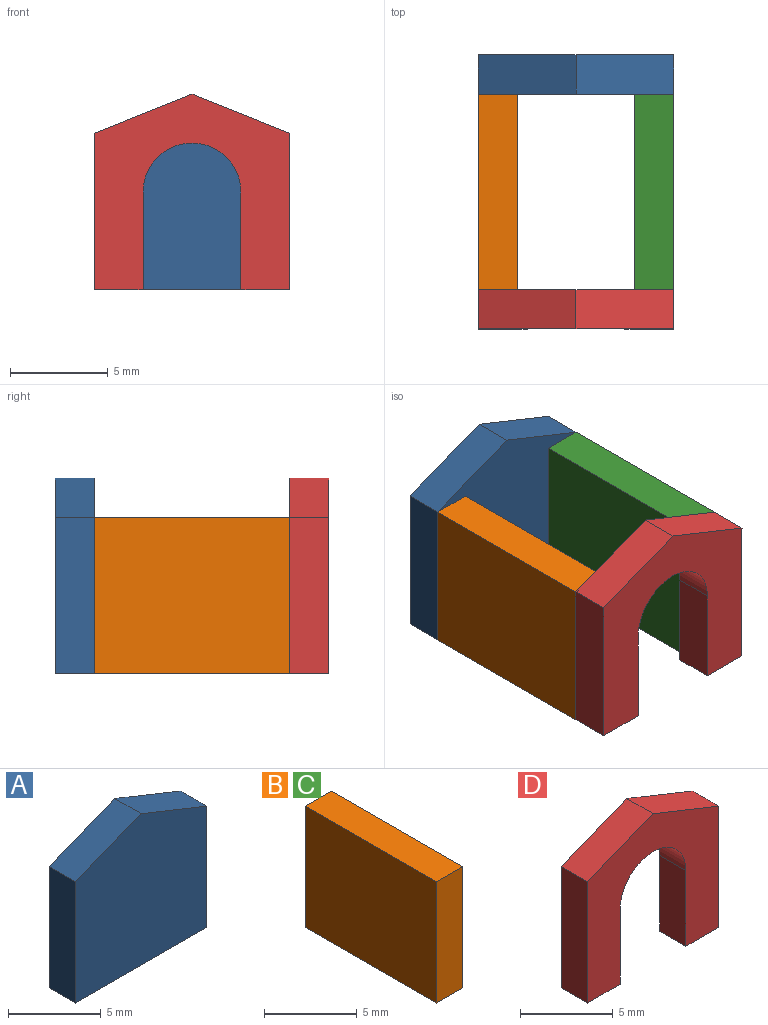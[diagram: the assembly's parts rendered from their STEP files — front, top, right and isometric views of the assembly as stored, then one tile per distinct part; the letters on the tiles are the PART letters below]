
ASSEMBLY  parts=4 mates=6
PART A: 7 faces, bbox 10x2x10 mm
  f0: plane 8x2mm, normal (-1,0,0), area 16mm2, adj f1,f4,f5,f6
  f1: plane 10x2mm, normal (0,0,-1), area 20mm2, adj f0,f2,f5,f6
  f2: plane 8x2mm, normal (1,0,0), area 16mm2, adj f1,f3,f5,f6
  f3: plane 5x2mm, normal (0.37,0,0.93), area 10.8mm2, adj f2,f4,f5,f6
  f4: plane 5x2mm, normal (-0.37,0,0.93), area 10.8mm2, adj f0,f3,f5,f6
  f5: plane 10x10mm, normal (0,-1,0), area 90mm2, adj f0,f1,f2,f3,f4
  f6: plane 10x10mm, normal (0,1,0), area 90mm2, adj f0,f1,f2,f3,f4
PART B: 6 faces, bbox 2x10x8 mm
  f0: plane 8x2mm, normal (0,1,0), area 16mm2, adj f1,f3,f4,f5
  f1: plane 10x2mm, normal (0,0,1), area 20mm2, adj f0,f2,f4,f5
  f2: plane 8x2mm, normal (0,-1,0), area 16mm2, adj f1,f3,f4,f5
  f3: plane 10x2mm, normal (0,0,-1), area 20mm2, adj f0,f2,f4,f5
  f4: plane 10x8mm, normal (1,0,0), area 80mm2, adj f0,f1,f2,f3
  f5: plane 10x8mm, normal (-1,0,0), area 80mm2, adj f0,f1,f2,f3
PART C: same geometry as B
PART D: 11 faces, bbox 10x2x10 mm
  f0: plane 2.5x2mm, normal (0,0,-1), area 5mm2, adj f1,f2,f5,f8
  f1: plane 10x10mm, normal (0,-1,0), area 55.2mm2, adj f0,f3,f4,f5,f6,f7,f8,f9
  f2: plane 10x10mm, normal (0,1,0), area 55.2mm2, adj f0,f3,f4,f5,f6,f7,f8,f9
  f3: plane 8x2mm, normal (-1,0,0), area 16mm2, adj f1,f2,f4,f7
  f4: plane 2.5x2mm, normal (0,0,-1), area 5mm2, adj f1,f2,f3,f10
  f5: plane 8x2mm, normal (1,0,0), area 16mm2, adj f0,f1,f2,f6
  f6: plane 5x2mm, normal (0.37,0,0.93), area 10.8mm2, adj f1,f2,f5,f7
  f7: plane 5x2mm, normal (-0.37,0,0.93), area 10.8mm2, adj f1,f2,f3,f6
  f8: plane 5x2mm, normal (-1,0,0), area 10mm2, adj f0,f1,f2,f9
  f9: cylinder r=2.5mm len=5mm, axis (0,-1,0), area 15.7mm2, adj f1,f2,f8,f10
  f10: plane 5x2mm, normal (1,0,0), area 10mm2, adj f1,f2,f4,f9
PLACE A rot(axis=(0.17,-0.08,-0.98),0deg) t=(66.21,-3.27,-6.07)mm
PLACE B rot(axis=(0.17,-0.08,-0.98),0deg) t=(26.3,1.48,-10.78)mm
PLACE C rot(axis=(0.17,-0.08,-0.98),0deg) t=(34.3,1.48,-10.78)mm
PLACE D rot(axis=(0.17,-0.08,-0.98),0deg) t=(69.22,-15.27,2.36)mm
MATE fastened D.f5 <-> C.f4  axis (1,0,0) through (36.3,-15.27,2.36)mm
MATE planar A.f5 <-> A.f5  axis (0,-1,0) through (31.3,-5.27,6.87)mm
MATE fastened B.f0 <-> B.f3  axis (0,1,0) through (27.3,-5.27,6.36)mm
MATE fastened B.f0 <-> B.f3  axis (0,1,0) through (26.3,-5.27,10.36)mm
MATE fastened B.f5 <-> A.f0  axis (-1,0,0) through (26.3,-5.27,10.36)mm
MATE fastened A.f2 <-> C.f4  axis (1,0,0) through (36.3,-5.27,2.36)mm
